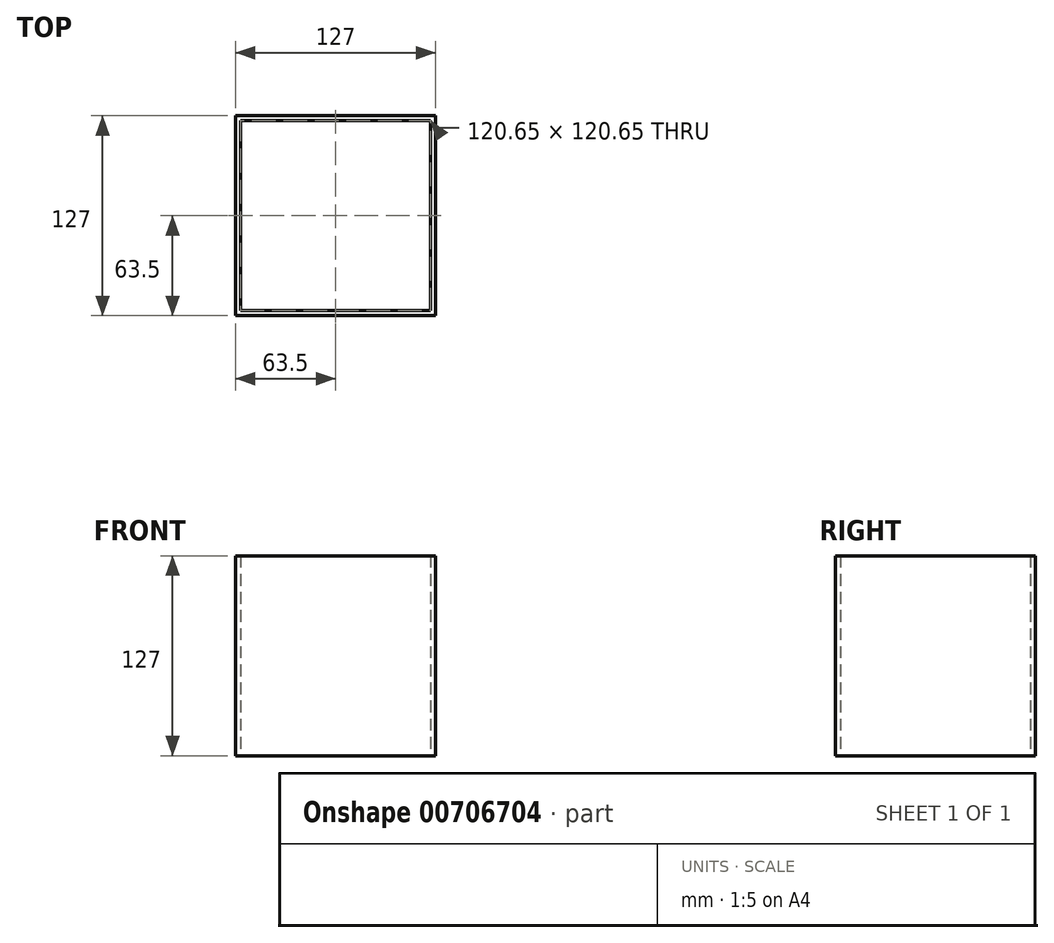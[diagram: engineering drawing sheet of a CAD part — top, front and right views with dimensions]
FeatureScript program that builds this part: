
annotation { "Feature Type Name" : "Feature", "Feature Type Description" : "" }
export const myFeature = defineFeature(function(context is Context, id is Id, definition is map)
    precondition{}
    {
        {
            var Q0;
            Q0=qCreatedBy(makeId("Top.planeOp"),FACE);
            var sketch = newSketch(context, id + "F0", { "sketchPlane" : qUnion([Q0])});
            skLineSegment(sketch, "E0.bottom", {"start": v(0, 0) * mm, "end": v(127, 0) * mm});
            skLineSegment(sketch, "E0.top", {"start": v(0, 127) * mm, "end": v(127, 127) * mm});
            skLineSegment(sketch, "E0.left", {"start": v(0, 0) * mm, "end": v(0, 127) * mm});
            skLineSegment(sketch, "E0.right", {"start": v(127, 0) * mm, "end": v(127, 127) * mm});
            skSolve(sketch);
        }
        {
            var Q0;
            Q0=makeQuery(id+"F0.imprint","IMPRINT",FACE,{"disambiguationData":[TD([[makeQuery(id+"F0.imprint","IMPRINT",EDGE,{"derivedFrom":sQuery(id+"F0.wireOp",EDGE,"E0.bottom")}),1.0]])]});
            extrude(context, id + "F1", {"entities" : qUnion([Q0]), "depth" : 127 * mm, "offsetDistance" : 25.4 * mm});
        }
        {
            var Q0;
            Q0=makeQuery(id+"F1.opExtrude","CAP_FACE",FACE,{"disambiguationData":[OSD([sQuery(id+"F0.wireOp",EDGE,"E0.bottom"),sQuery(id+"F0.wireOp",EDGE,"E0.top"),sQuery(id+"F0.wireOp",EDGE,"E0.left"),sQuery(id+"F0.wireOp",EDGE,"E0.right")])],"isStart":false});
            var Q1;
            Q1=makeQuery(id+"F1.opExtrude","CAP_FACE",FACE,{"disambiguationData":[OSD([sQuery(id+"F0.wireOp",EDGE,"E0.bottom"),sQuery(id+"F0.wireOp",EDGE,"E0.top"),sQuery(id+"F0.wireOp",EDGE,"E0.left"),sQuery(id+"F0.wireOp",EDGE,"E0.right")])],"isStart":true});
            shell(context, id + "F2", {"entities" : qUnion([Q0, Q1]), "thickness" : 3.17 * mm});
        }
    });
